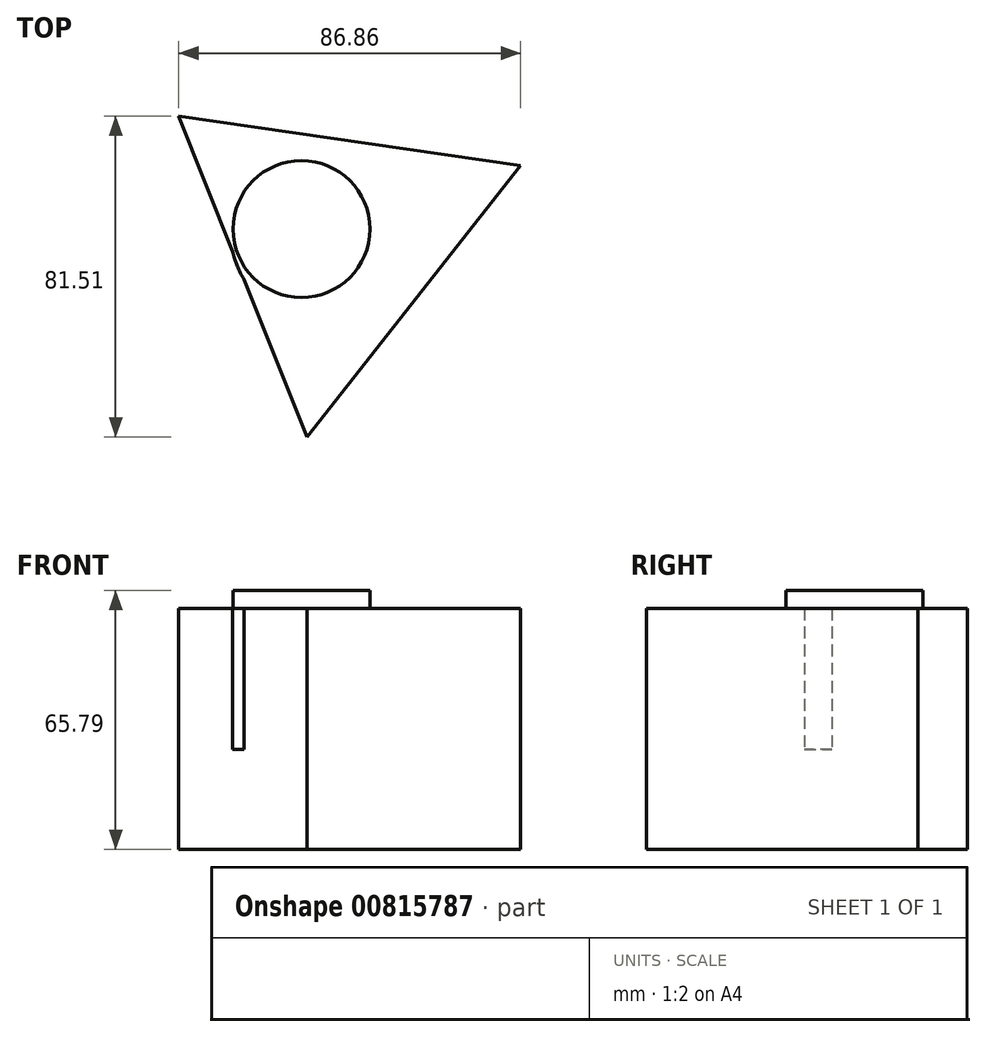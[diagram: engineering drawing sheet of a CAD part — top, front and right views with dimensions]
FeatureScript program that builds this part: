
annotation { "Feature Type Name" : "Feature", "Feature Type Description" : "" }
export const myFeature = defineFeature(function(context is Context, id is Id, definition is map)
    precondition{}
    {
        {
            var Q0;
            Q0=qCreatedBy(makeId("Top.planeOp"),FACE);
            var sketch = newSketch(context, id + "F0", { "sketchPlane" : qUnion([Q0])});
            skCircle(sketch, "E0.cCircle", {"center": v(-28.41, 40.8) * mm, "radius": 25.33 * mm, "construction": true});
            skLineSegment(sketch, "E0.0", {"start": v(18.65, 59.59) * mm, "end": v(-35.68, -9.34) * mm});
            skLineSegment(sketch, "E0.1", {"start": v(-35.68, -9.34) * mm, "end": v(-68.2, 72.17) * mm});
            skLineSegment(sketch, "E0.2", {"start": v(-68.2, 72.17) * mm, "end": v(18.65, 59.59) * mm});
            skPoint(sketch, "E0.0.midPoint", {"position": v(-8.52, 25.12) * mm});
            skSolve(sketch);
        }
        {
            var Q0;
            Q0 = qSketchRegion(id + "F0", true);
            extrude(context, id + "F1", {"entities" : qUnion([Q0]), "depth" : 25.4 * mm, "offsetDistance" : 25.4 * mm});
        }
        {
            var Q0;
            Q0=makeQuery(id+"F1.opExtrude","CAP_FACE",FACE,{"disambiguationData":[OSD([sQuery(id+"F0.wireOp",EDGE,"E0.0"),sQuery(id+"F0.wireOp",EDGE,"E0.1"),sQuery(id+"F0.wireOp",EDGE,"E0.2")])],"isStart":false});
            var sketch = newSketch(context, id + "F2", { "sketchPlane" : qUnion([Q0])});
            skCircle(sketch, "E1", {"center": v(-31.78, 42.74) * mm, "radius": 23.24 * mm});
            skSolve(sketch);
        }
        {
            var Q0;
            {var subQ0=sQuery(id+"F2.wireOp",EDGE,"E1");var subQ1=makeQuery(id+"F1.opExtrude","CAP_EDGE",EDGE,{"disambiguationData":[OSD([sQuery(id+"F0.wireOp",EDGE,"E0.1")])],"isStart":false});var subQ2=makeQuery(id+"F2.imprint","INTERSECT",VERTEX,{"disambiguationData":[OD(0.0)],"derivedFrom":[subQ1,subQ0]});Q0=makeQuery(id+"F2.imprint","IMPRINT",FACE,{"disambiguationData":[TD([[makeQuery(id+"F2.imprint","IMPRINT",EDGE,{"disambiguationData":[TD([[subQ2,1.0]])],"derivedFrom":subQ0}),1.0]])]});}
            var Q1;
            {var subQ1=makeQuery(id+"F1.opExtrude","CAP_EDGE",EDGE,{"disambiguationData":[OSD([sQuery(id+"F0.wireOp",EDGE,"E0.0")])],"isStart":false});Q1=makeQuery(id+"F2.imprint","IMPRINT",FACE,{"disambiguationData":[TD([[makeQuery(id+"F2.imprint","IMPRINT",EDGE,{"derivedFrom":subQ1}),-1.0]])]});}
            var Q2;
            {var subQ0=sQuery(id+"F2.wireOp",EDGE,"E1");var subQ1=makeQuery(id+"F1.opExtrude","CAP_EDGE",EDGE,{"disambiguationData":[OSD([sQuery(id+"F0.wireOp",EDGE,"E0.1")])],"isStart":false});var subQ2=makeQuery(id+"F2.imprint","INTERSECT",VERTEX,{"disambiguationData":[OD(0.0)],"derivedFrom":[subQ1,subQ0]});Q2=makeQuery(id+"F2.imprint","IMPRINT",FACE,{"disambiguationData":[TD([[makeQuery(id+"F2.imprint","IMPRINT",EDGE,{"disambiguationData":[TD([[subQ2,-1.0]])],"derivedFrom":subQ0}),1.0]])]});}
            extrude(context, id + "F3", {"entities" : qUnion([Q0, Q1, Q2]), "operationType" : NewBodyOperationType.ADD, "depth" : 35.81 * mm, "offsetDistance" : 25.4 * mm});
        }
        {
            var Q0;
            Q0=makeQuery(id+"F3.opExtrude","CAP_FACE",FACE,{"disambiguationData":[OSD([sQuery(id+"F0.wireOp",EDGE,"E0.0"),sQuery(id+"F0.wireOp",EDGE,"E0.1"),sQuery(id+"F0.wireOp",EDGE,"E0.2"),sQuery(id+"F2.wireOp",EDGE,"E1")])],"isStart":false});
            var sketch = newSketch(context, id + "F4", { "sketchPlane" : qUnion([Q0])});
            skCircle(sketch, "E2", {"center": v(-37.02, 43.47) * mm, "radius": 17.38 * mm});
            skSolve(sketch);
        }
        {
            var Q0;
            Q0 = qSketchRegion(id + "F4", true);
            extrude(context, id + "F5", {"entities" : qUnion([Q0]), "operationType" : NewBodyOperationType.ADD, "depth" : 4.57 * mm, "offsetDistance" : 25.4 * mm});
        }
    });
